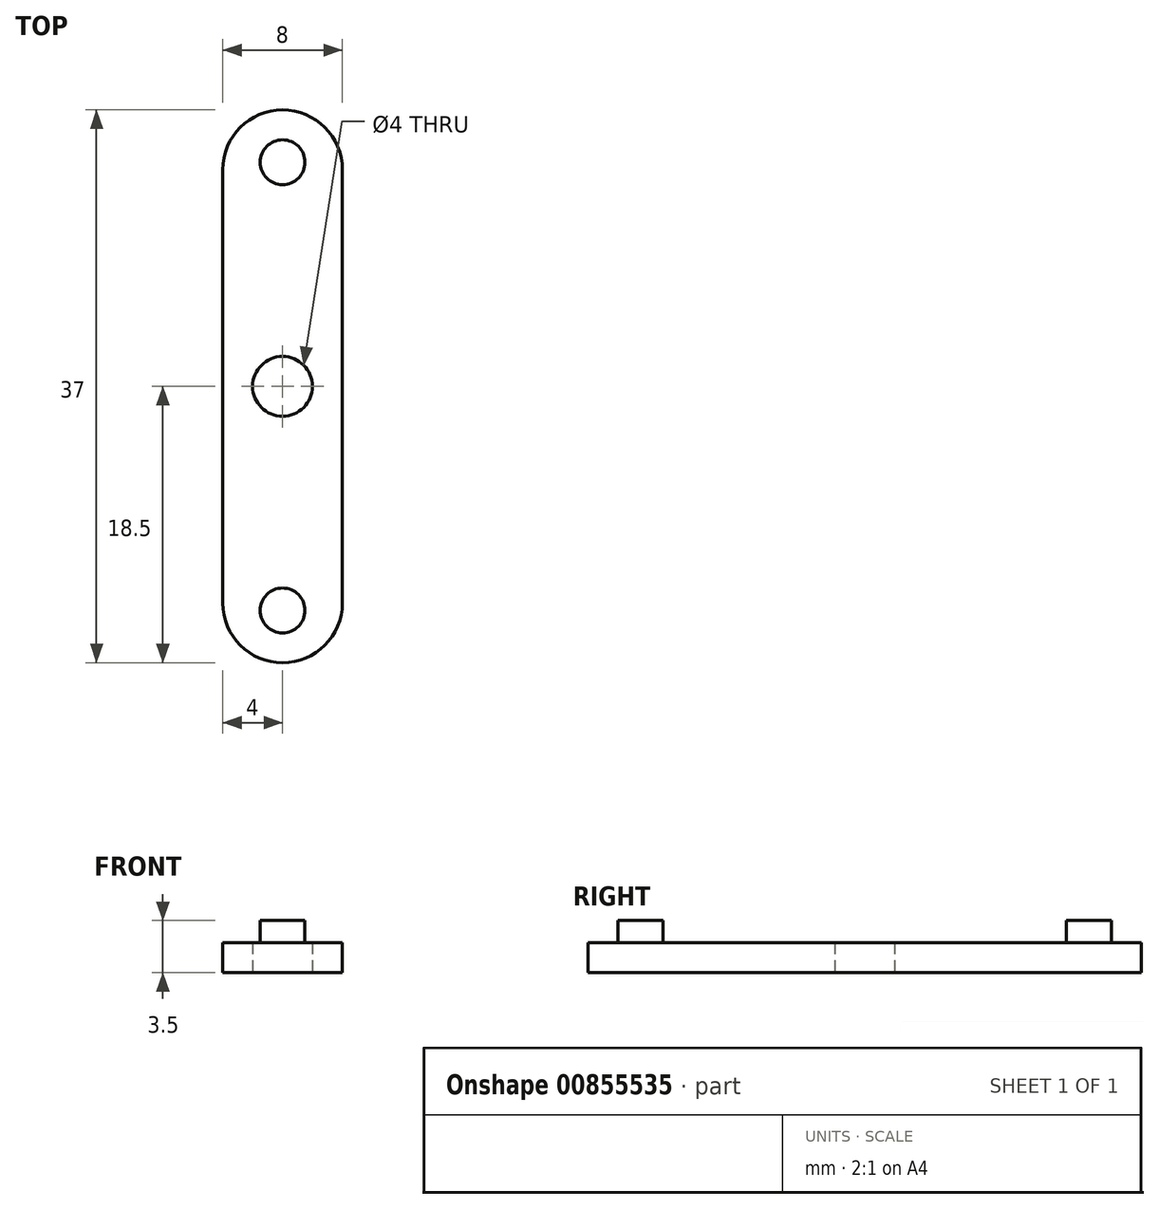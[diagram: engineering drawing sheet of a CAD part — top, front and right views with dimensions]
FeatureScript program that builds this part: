
annotation { "Feature Type Name" : "Feature", "Feature Type Description" : "" }
export const myFeature = defineFeature(function(context is Context, id is Id, definition is map)
    precondition{}
    {
        {
            var Q0;
            Q0=qCreatedBy(makeId("Top.planeOp"),FACE);
            var sketch = newSketch(context, id + "F0", { "sketchPlane" : qUnion([Q0])});
            skLineSegment(sketch, "E0.bottom", {"start": v(-4, 18.5) * mm, "end": v(4, 18.5) * mm});
            skLineSegment(sketch, "E0.top", {"start": v(-4, -18.5) * mm, "end": v(4, -18.5) * mm});
            skLineSegment(sketch, "E0.left", {"start": v(-4, 18.5) * mm, "end": v(-4, -18.5) * mm});
            skLineSegment(sketch, "E0.right", {"start": v(4, 18.5) * mm, "end": v(4, -18.5) * mm});
            skPoint(sketch, "E0.middle", {"position": v(0, 0) * mm});
            skCircle(sketch, "E1", {"center": v(0, 0) * mm, "radius": 2 * mm});
            skSolve(sketch);
        }
        {
            var Q0;
            Q0=makeQuery(id+"F0.imprint","IMPRINT",FACE,{"disambiguationData":[TD([[makeQuery(id+"F0.imprint","IMPRINT",EDGE,{"derivedFrom":sQuery(id+"F0.wireOp",EDGE,"E0.bottom")}),-1.0]])]});
            extrude(context, id + "F1", {"entities" : qUnion([Q0]), "depth" : 2 * mm, "offsetDistance" : 25 * mm});
        }
        {
            var Q0;
            Q0=makeQuery(id+"F1.opExtrude","CAP_FACE",FACE,{"disambiguationData":[OSD([sQuery(id+"F0.wireOp",EDGE,"E0.bottom"),sQuery(id+"F0.wireOp",EDGE,"E0.top"),sQuery(id+"F0.wireOp",EDGE,"E0.left"),sQuery(id+"F0.wireOp",EDGE,"E0.right"),sQuery(id+"F0.wireOp",EDGE,"E1")])],"isStart":false});
            var sketch = newSketch(context, id + "F2", { "sketchPlane" : qUnion([Q0])});
            skCircle(sketch, "E2", {"center": v(0, 15) * mm, "radius": 1.5 * mm});
            skCircle(sketch, "E3", {"center": v(0, -15) * mm, "radius": 1.5 * mm});
            skSolve(sketch);
        }
        {
            var Q0;
            Q0 = qSketchRegion(id + "F2", true);
            extrude(context, id + "F3", {"entities" : qUnion([Q0]), "operationType" : NewBodyOperationType.ADD, "depth" : 1.5 * mm, "offsetDistance" : 25 * mm});
        }
        {
            var Q0;
            Q0=makeQuery(id+"F1.opExtrude","SWEPT_EDGE",EDGE,{"disambiguationData":[OSD([sQuery(id+"F0.wireOp",EDGE,"E0.bottom"),sQuery(id+"F0.wireOp",EDGE,"E0.left")])]});
            var Q1;
            Q1=makeQuery(id+"F1.opExtrude","SWEPT_EDGE",EDGE,{"disambiguationData":[OSD([sQuery(id+"F0.wireOp",EDGE,"E0.bottom"),sQuery(id+"F0.wireOp",EDGE,"E0.right")])]});
            var Q2;
            Q2=makeQuery(id+"F1.opExtrude","SWEPT_EDGE",EDGE,{"disambiguationData":[OSD([sQuery(id+"F0.wireOp",EDGE,"E0.top"),sQuery(id+"F0.wireOp",EDGE,"E0.right")])]});
            var Q3;
            Q3=makeQuery(id+"F1.opExtrude","SWEPT_EDGE",EDGE,{"disambiguationData":[OSD([sQuery(id+"F0.wireOp",EDGE,"E0.top"),sQuery(id+"F0.wireOp",EDGE,"E0.left")])]});
            fillet(context, id + "F4", {"entities" : qUnion([Q0, Q1, Q2, Q3]), "tangentPropagation" : true, "radius" : 4 * mm, "defaultsChanged" : true, "vertexSettings" : [], "allowEdgeOverflow" : false});
        }
    });
